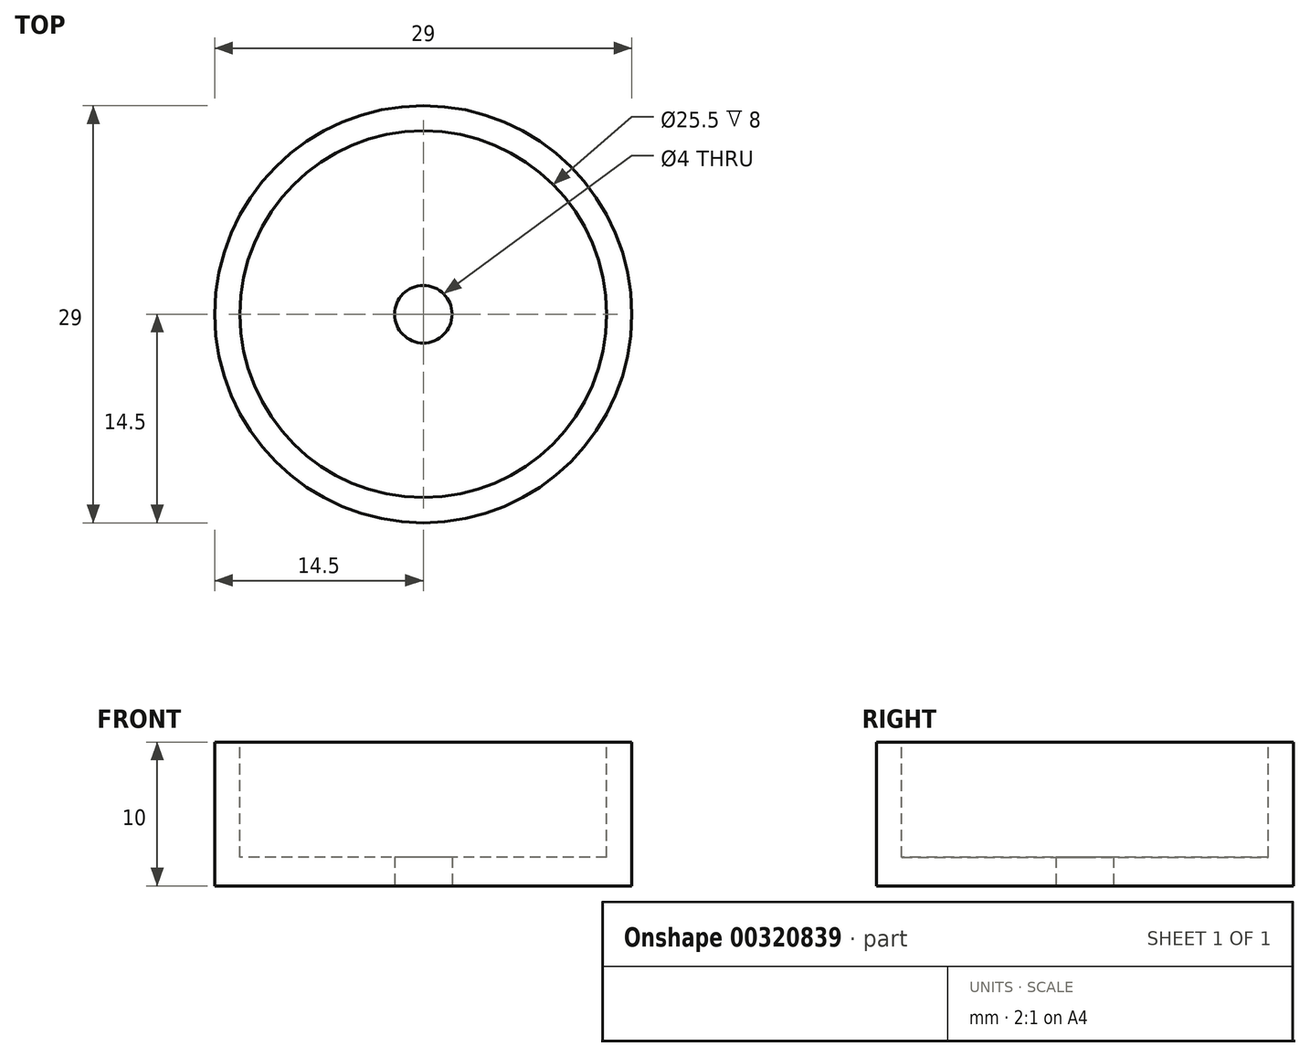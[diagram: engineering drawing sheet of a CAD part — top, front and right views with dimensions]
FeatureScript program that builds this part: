
annotation { "Feature Type Name" : "Feature", "Feature Type Description" : "" }
export const myFeature = defineFeature(function(context is Context, id is Id, definition is map)
    precondition{}
    {
        {
            var Q0;
            Q0=qCreatedBy(makeId("Top.planeOp"),FACE);
            var sketch = newSketch(context, id + "F0", { "sketchPlane" : qUnion([Q0])});
            skCircle(sketch, "E0", {"center": v(0, 0) * mm, "radius": 14.5 * mm});
            skSolve(sketch);
        }
        {
            var Q0;
            Q0 = qSketchRegion(id + "F0", true);
            extrude(context, id + "F1", {"entities" : qUnion([Q0]), "depth" : 10 * mm});
        }
        {
            var Q0;
            Q0=makeQuery(id+"F1.opExtrude","CAP_FACE",FACE,{"disambiguationData":[OSD([sQuery(id+"F0.wireOp",EDGE,"E0")])],"isStart":false});
            var sketch = newSketch(context, id + "F2", { "sketchPlane" : qUnion([Q0])});
            skCircle(sketch, "E1", {"center": v(0, 0) * mm, "radius": 12.75 * mm});
            skSolve(sketch);
        }
        {
            var Q0;
            Q0 = qSketchRegion(id + "F2", true);
            extrude(context, id + "F3", {"entities" : qUnion([Q0]), "operationType" : NewBodyOperationType.REMOVE, "oppositeDirection" : true, "depth" : 8 * mm});
        }
        {
            var Q0;
            Q0=qCreatedBy(makeId("Top.planeOp"),FACE);
            var sketch = newSketch(context, id + "F4", { "sketchPlane" : qUnion([Q0])});
            skCircle(sketch, "E2", {"center": v(0, 0) * mm, "radius": 2 * mm});
            skSolve(sketch);
        }
        {
            var Q0;
            Q0 = qSketchRegion(id + "F4", true);
            extrude(context, id + "F5", {"entities" : qUnion([Q0]), "operationType" : NewBodyOperationType.REMOVE, "depth" : 2 * mm});
        }
    });
